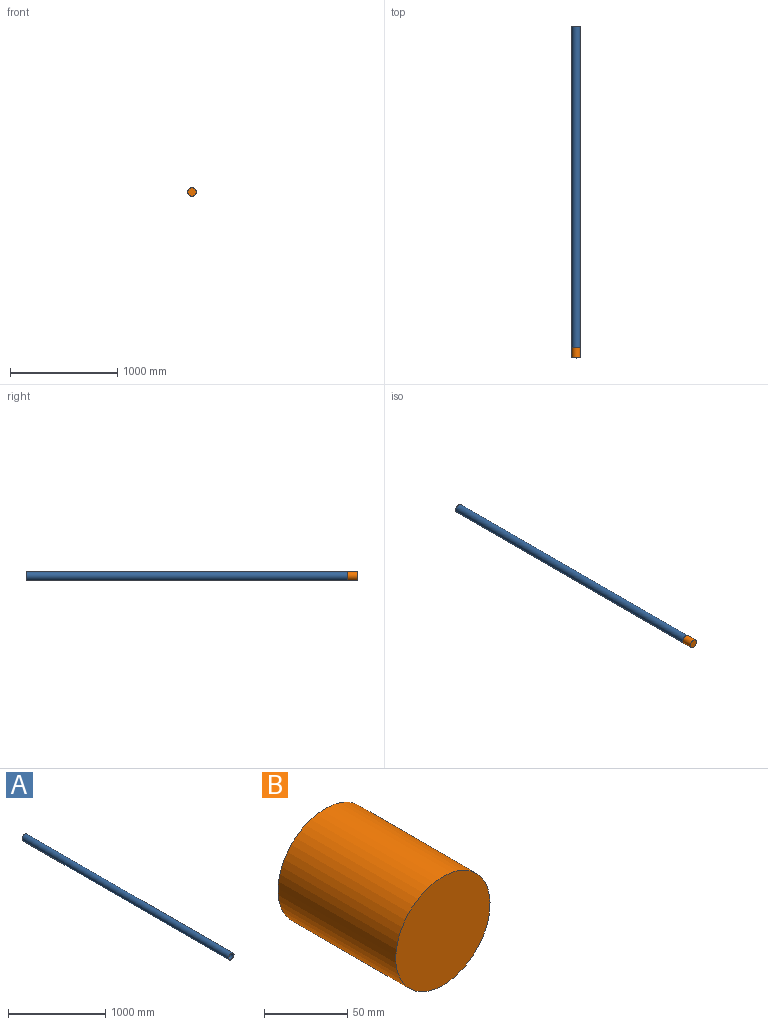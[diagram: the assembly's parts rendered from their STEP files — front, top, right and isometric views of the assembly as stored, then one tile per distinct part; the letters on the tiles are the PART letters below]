
ASSEMBLY  parts=2 mates=1
PART A: 4 faces, bbox 80x3000x80 mm
  f0: cylinder r=35mm len=3000mm, axis (0,1,0), area 659734.5mm2, adj f2,f3
  f1: cylinder r=40mm len=3000mm, axis (0,1,0), area 753982.2mm2, adj f2,f3
  f2: plane 80x80mm, normal (0,-1,0), area 1178.1mm2, adj f0,f1
  f3: plane 80x80mm, normal (0,1,0), area 1178.1mm2, adj f0,f1
PART B: 3 faces, bbox 80x100x80 mm
  f0: cylinder r=40mm len=100mm, axis (0,1,0), area 25132.7mm2, adj f1,f2
  f1: plane 80x80mm, normal (0,-1,0), area 5026.5mm2, adj f0
  f2: plane 80x80mm, normal (0,1,0), area 5026.5mm2, adj f0
PLACE A t=(0,1949,0)mm
PLACE B t=(0,-1051,0)mm
MATE fastened A.f1 <-> B.f0  axis (0,-1,0) through (0,-1051,0)mm
